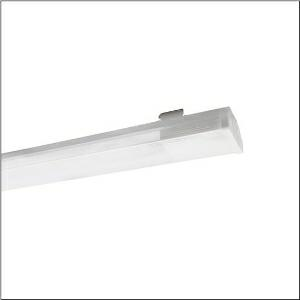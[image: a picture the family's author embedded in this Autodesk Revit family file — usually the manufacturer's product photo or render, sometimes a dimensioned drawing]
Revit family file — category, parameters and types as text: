
# Revit family: modario_31_gen_2_53bm813du4f5c2_6de7
name_source: partatom
category: Lighting Fixtures
units: mm (PartAtom-declared; Revit-internal decimal feet)

## family parameters
Cut with Voids When Loaded = No
Host = Face
Light Source = No
Part Type = Normal
Room Calculation Point = No
Round Connector Dimension = Use Diameter
Shared = No

## types (1)
- --- (1 x LED, 15920 lm, 92.1 W, 4000K)
    Apparent Load = 92 VA
    CIE Flux Codes = 62 83 95 93 100
    Color Rendering = 80
    Color Temperature = 4000K
    Default Elevation = 1800 mm
    Description = Modario 31 Gen.2, luminaire insert, of sheet steel, coil coated, white, length: 2.392mm, width: 81mm, height: 82mm, 8x system unit, system units: 299mm, LED rated luminous flux: 15.920lm, light colour: 840, SDCM (Standard Deviation of Colour Matching)MacAdam ≤ 3 SDCM (initial), control gear: DALI 2, control gear: ECG DALI, with plug, 5-pole, with phase selection, mains connection: 220..240V, AC, 50/60Hz, rated input power: 92W, through-wiring accessed according to module size, primary optical cover: cover, of PMMA, light emission: direct distribution, primary light characteristic: symmetric, protection rating (complete): IP20, protection rating (LED compartment): IP50, insulation class (complete): insulation class I (protective earthing), certification: CE, ENEC, VDE, UKCA, impact resistance: IK03, permissible ambient temperature for indoor applications: -25..+40°C, corresponds to IFS (International Featured Standards) requirements for safety and quality in the food industry, reducing of maximum allowable ambient temperature of 5°C with ceiling mounting, IP40 when using the optional accessory 5TP9018, packaging unit: 1 piece
    Height = 92 mm
    Lamp = 1 x LED
    Lamp Light Flux = 15920 lm
    Lamp Power = 92.1 W
    Lamp count = 1
    Length = 2392 mm
    Luminous efficacy = 173 lm/W
    Manufacturer = Siteco
    ModVariant = No
    Model = 53BM813DU4F5C2
    Mounting Place = Ceiling
    Mounting Type = Pendant
    Number of Poles = 1
    OnlyDefault = Yes
    Power Factor = 1
    Product Name = Modario 31 Gen.2
    Product group = luminaire insert | ceiling pendant
    ProductGroupID = 901
    Protection Class = Protection class I
    Protection Degree = IP 20
    RLX_Detail_Level = 1
    RLX_Emergency_Light_Flux = 0 lm
    RLX_Emergency_Type = 0
    RLX_Emergency_Type_DB = No
    RlxData = <blob elided: 38301 chars, md5=298ee50e>
    Socket = socket
    Standby Power = 0 W
    System Light Flux = 15920 lm
    System Power = 92 W
    Type Comments = factory setting: luminous flux: 100 % | dim-lin: 254 | 418 mA
    Type Image = l_1341883.jpg
    URL = http://relux.com
    VarID = @adj_051397
    Voltage = 0 V
    Weight = 0.00 kg
    Width = 81 mm

## geometry (parser evidence)
native form markers: Blend x4, Sweep x11
no freeform markers — native parametric forms only
